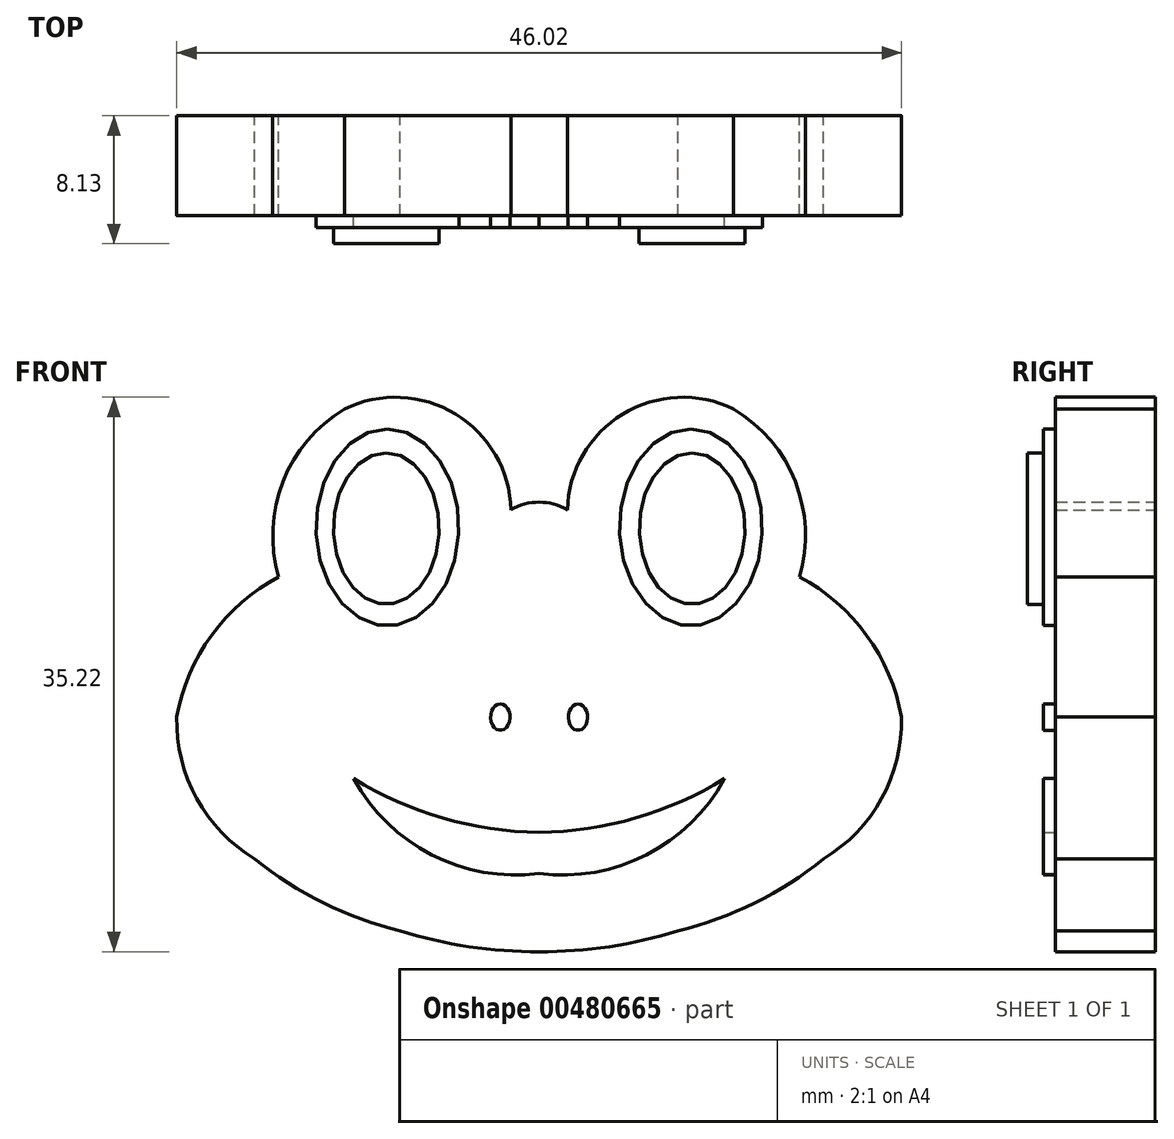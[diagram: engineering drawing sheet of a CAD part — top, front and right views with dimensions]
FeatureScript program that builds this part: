
annotation { "Feature Type Name" : "Feature", "Feature Type Description" : "" }
export const myFeature = defineFeature(function(context is Context, id is Id, definition is map)
    precondition{}
    {
        {
            var Q0;
            Q0=qCreatedBy(makeId("Front.planeOp"),FACE);
            var sketch = newSketch(context, id + "F0", { "sketchPlane" : qUnion([Q0])});
            skArc(sketch, "E0", {"start": v(-1.8, 13.16) * mm, "mid": v(-5.32, 19.25) * mm, "end": v(-12.34, 19.58) * mm});
            skArc(sketch, "E1", {"start": v(-12.34, 19.58) * mm, "mid": v(-16.27, 14.96) * mm, "end": v(-16.53, 8.9) * mm});
            skArc(sketch, "E2", {"start": v(-16.53, 8.9) * mm, "mid": v(-20.8, 5.2) * mm, "end": v(-23.01, 0) * mm});
            skArc(sketch, "E3", {"start": v(-23.01, 0) * mm, "mid": v(-21.75, -5.17) * mm, "end": v(-18.06, -9) * mm});
            skArc(sketch, "E4", {"start": v(-18.06, -9) * mm, "mid": v(-13.7, -11.8) * mm, "end": v(-8.82, -13.57) * mm});
            skArc(sketch, "E5", {"start": v(-8.82, -13.57) * mm, "mid": v(-4.46, -14.58) * mm, "end": v(0, -14.9) * mm});
            skArc(sketch, "E6.MirrorCS", {"start": v(1.8, 13.16) * mm, "mid": v(5.32, 19.25) * mm, "end": v(12.34, 19.58) * mm});
            skArc(sketch, "E7.MirrorCS", {"start": v(12.34, 19.58) * mm, "mid": v(16.27, 14.96) * mm, "end": v(16.53, 8.9) * mm});
            skArc(sketch, "E8.MirrorCS", {"start": v(16.53, 8.9) * mm, "mid": v(20.8, 5.2) * mm, "end": v(23.01, 0) * mm});
            skArc(sketch, "E9.MirrorCS", {"start": v(23.01, 0) * mm, "mid": v(21.75, -5.17) * mm, "end": v(18.06, -9) * mm});
            skArc(sketch, "E10.MirrorCS", {"start": v(18.06, -9) * mm, "mid": v(13.7, -11.8) * mm, "end": v(8.82, -13.57) * mm});
            skArc(sketch, "E11.MirrorCS", {"start": v(8.82, -13.57) * mm, "mid": v(4.46, -14.58) * mm, "end": v(0, -14.9) * mm});
            skArc(sketch, "E12", {"start": v(1.8, 13.16) * mm, "mid": v(0, 13.66) * mm, "end": v(-1.8, 13.16) * mm});
            skSolve(sketch);
        }
        {
            var Q0;
            Q0 = qSketchRegion(id + "F0", true);
            extrude(context, id + "F1", {"entities" : qUnion([Q0]), "depth" : 6.35 * mm});
        }
        {
            var Q0;
            Q0=qCreatedBy(makeId("Front.planeOp"),FACE);
            var sketch = newSketch(context, id + "F2", { "sketchPlane" : qUnion([Q0])});
            skEllipse(sketch, "E13", {"center": v(-9.64, 12.05) * mm, "majorRadius": 6.24 * mm, "minorRadius": 4.54 * mm, "majorAxis": v(0, 1)});
            skEllipse(sketch, "E14", {"center": v(-2.47, 0) * mm, "majorRadius": 0.83 * mm, "minorRadius": 0.62 * mm, "majorAxis": v(0, 1)});
            skEllipse(sketch, "E15.MirrorC", {"center": v(9.64, 12.05) * mm, "majorRadius": 6.24 * mm, "minorRadius": 4.54 * mm, "majorAxis": v(0, 1)});
            skEllipse(sketch, "E16.MirrorC", {"center": v(2.47, 0) * mm, "majorRadius": 0.83 * mm, "minorRadius": 0.62 * mm, "majorAxis": v(0, 1)});
            skArc(sketch, "E17", {"start": v(-11.78, -3.9) * mm, "mid": v(-6.12, -6.4) * mm, "end": v(0, -7.32) * mm});
            skArc(sketch, "E18", {"start": v(-11.78, -3.9) * mm, "mid": v(-6.82, -8.74) * mm, "end": v(0, -9.92) * mm});
            skArc(sketch, "E19.MirrorCS", {"start": v(11.78, -3.9) * mm, "mid": v(6.12, -6.4) * mm, "end": v(0, -7.32) * mm});
            skArc(sketch, "E20.MirrorCS", {"start": v(11.78, -3.9) * mm, "mid": v(6.82, -8.74) * mm, "end": v(0, -9.92) * mm});
            skSolve(sketch);
        }
        {
            var Q0;
            Q0 = qSketchRegion(id + "F2", true);
            extrude(context, id + "F3", {"entities" : qUnion([Q0]), "operationType" : NewBodyOperationType.ADD, "depth" : 7.11 * mm});
        }
        {
            var Q0;
            Q0=qCreatedBy(makeId("Front.planeOp"),FACE);
            var sketch = newSketch(context, id + "F4", { "sketchPlane" : qUnion([Q0])});
            skEllipse(sketch, "E21", {"center": v(-9.71, 11.98) * mm, "majorRadius": 4.81 * mm, "minorRadius": 3.36 * mm, "majorAxis": v(0, 1)});
            skEllipse(sketch, "E22.MirrorC", {"center": v(9.71, 11.98) * mm, "majorRadius": 4.81 * mm, "minorRadius": 3.36 * mm, "majorAxis": v(0, 1)});
            skSolve(sketch);
        }
        {
            var Q0;
            Q0 = qSketchRegion(id + "F4", true);
            extrude(context, id + "F5", {"entities" : qUnion([Q0]), "operationType" : NewBodyOperationType.ADD, "depth" : 7.62 * mm});
        }
        {
            var Q0;
            Q0 = qSketchRegion(id + "F4", true);
            extrude(context, id + "F6", {"entities" : qUnion([Q0]), "operationType" : NewBodyOperationType.ADD, "depth" : 8.13 * mm});
        }
    });
